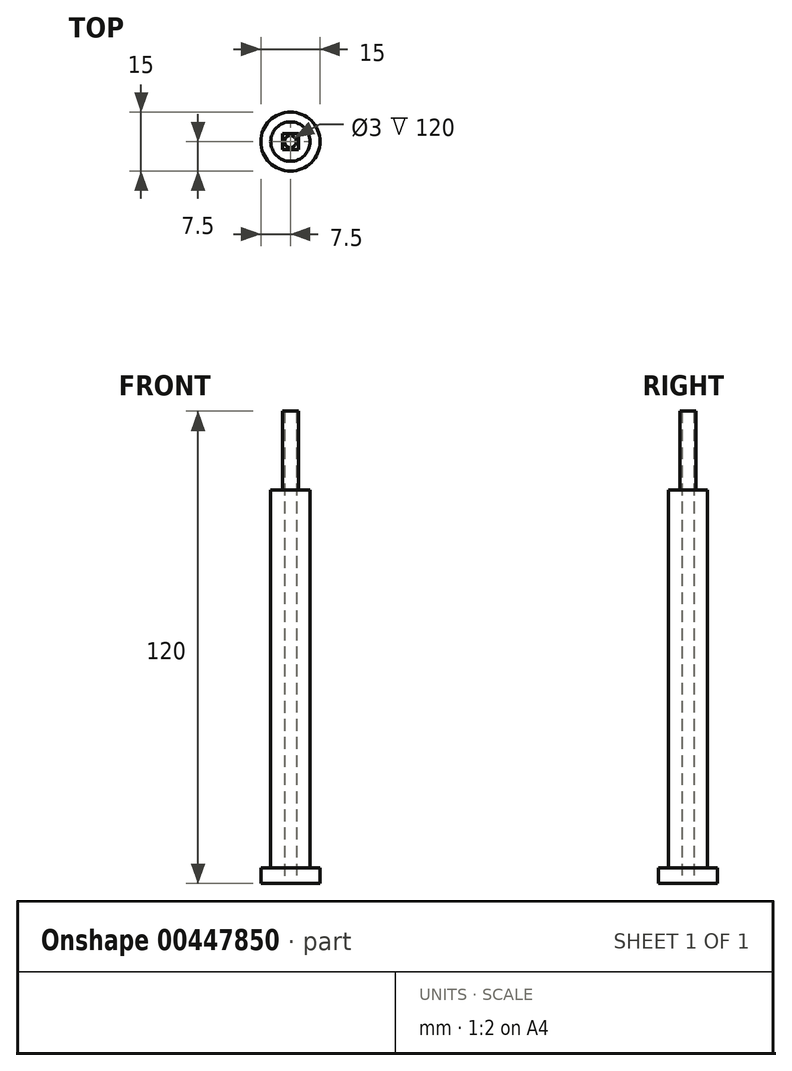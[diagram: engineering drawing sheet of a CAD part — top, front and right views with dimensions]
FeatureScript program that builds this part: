
annotation { "Feature Type Name" : "Feature", "Feature Type Description" : "" }
export const myFeature = defineFeature(function(context is Context, id is Id, definition is map)
    precondition{}
    {
        {
            var Q0;
            Q0=qCreatedBy(makeId("Top.planeOp"),FACE);
            var sketch = newSketch(context, id + "F0", { "sketchPlane" : qUnion([Q0])});
            skCircle(sketch, "E0", {"center": v(0, 0) * mm, "radius": 7.5 * mm});
            skSolve(sketch);
        }
        {
            var Q0;
            Q0=qSketchRegion(id+"F0",true);
            extrude(context, id + "F1", {"entities" : qUnion([Q0]), "depth" : 4 * mm});
        }
        {
            var Q0;
            Q0=qCreatedBy(makeId("Top.planeOp"),FACE);
            var sketch = newSketch(context, id + "F2", { "sketchPlane" : qUnion([Q0])});
            skCircle(sketch, "E1", {"center": v(0, 0) * mm, "radius": 5 * mm});
            skSolve(sketch);
        }
        {
            var Q0;
            Q0=qSketchRegion(id+"F2",true);
            extrude(context, id + "F3", {"entities" : qUnion([Q0]), "operationType" : NewBodyOperationType.ADD, "depth" : 100 * mm});
        }
        {
            var Q0;
            Q0=makeQuery(id+"F3.opExtrude","CAP_FACE",FACE,{"disambiguationData":[OSD([sQuery(id+"F2.wireOp",EDGE,"E1")])],"isStart":false});
            var sketch = newSketch(context, id + "F4", { "sketchPlane" : qUnion([Q0])});
            skLineSegment(sketch, "E2.bottom", {"start": v(-2, 2) * mm, "end": v(2, 2) * mm});
            skLineSegment(sketch, "E2.top", {"start": v(-2, -2) * mm, "end": v(2, -2) * mm});
            skLineSegment(sketch, "E2.left", {"start": v(-2, 2) * mm, "end": v(-2, -2) * mm});
            skLineSegment(sketch, "E2.right", {"start": v(2, 2) * mm, "end": v(2, -2) * mm});
            skSolve(sketch);
        }
        {
            var Q0;
            Q0=makeQuery(id+"F4.imprint","IMPRINT",FACE,{"disambiguationData":[TD([[makeQuery(id+"F4.imprint","IMPRINT",EDGE,{"derivedFrom":sQuery(id+"F4.wireOp",EDGE,"E2.bottom")}),-1.0]])]});
            extrude(context, id + "F5", {"entities" : qUnion([Q0]), "operationType" : NewBodyOperationType.ADD, "depth" : 20 * mm});
        }
        {
            var Q0;
            Q0=makeQuery(id+"F1.opExtrude","CAP_FACE",FACE,{"disambiguationData":[OSD([sQuery(id+"F0.wireOp",EDGE,"E0")])],"isStart":true});
            var sketch = newSketch(context, id + "F6", { "sketchPlane" : qUnion([Q0])});
            skCircle(sketch, "E3", {"center": v(0, 0) * mm, "radius": 1.5 * mm});
            skSolve(sketch);
        }
        {
            var Q0;
            Q0 = qSketchRegion(id + "F6", true);
            extrude(context, id + "F7", {"entities" : qUnion([Q0]), "operationType" : NewBodyOperationType.REMOVE, "oppositeDirection" : true, "depth" : 122.4 * mm});
        }
    });
